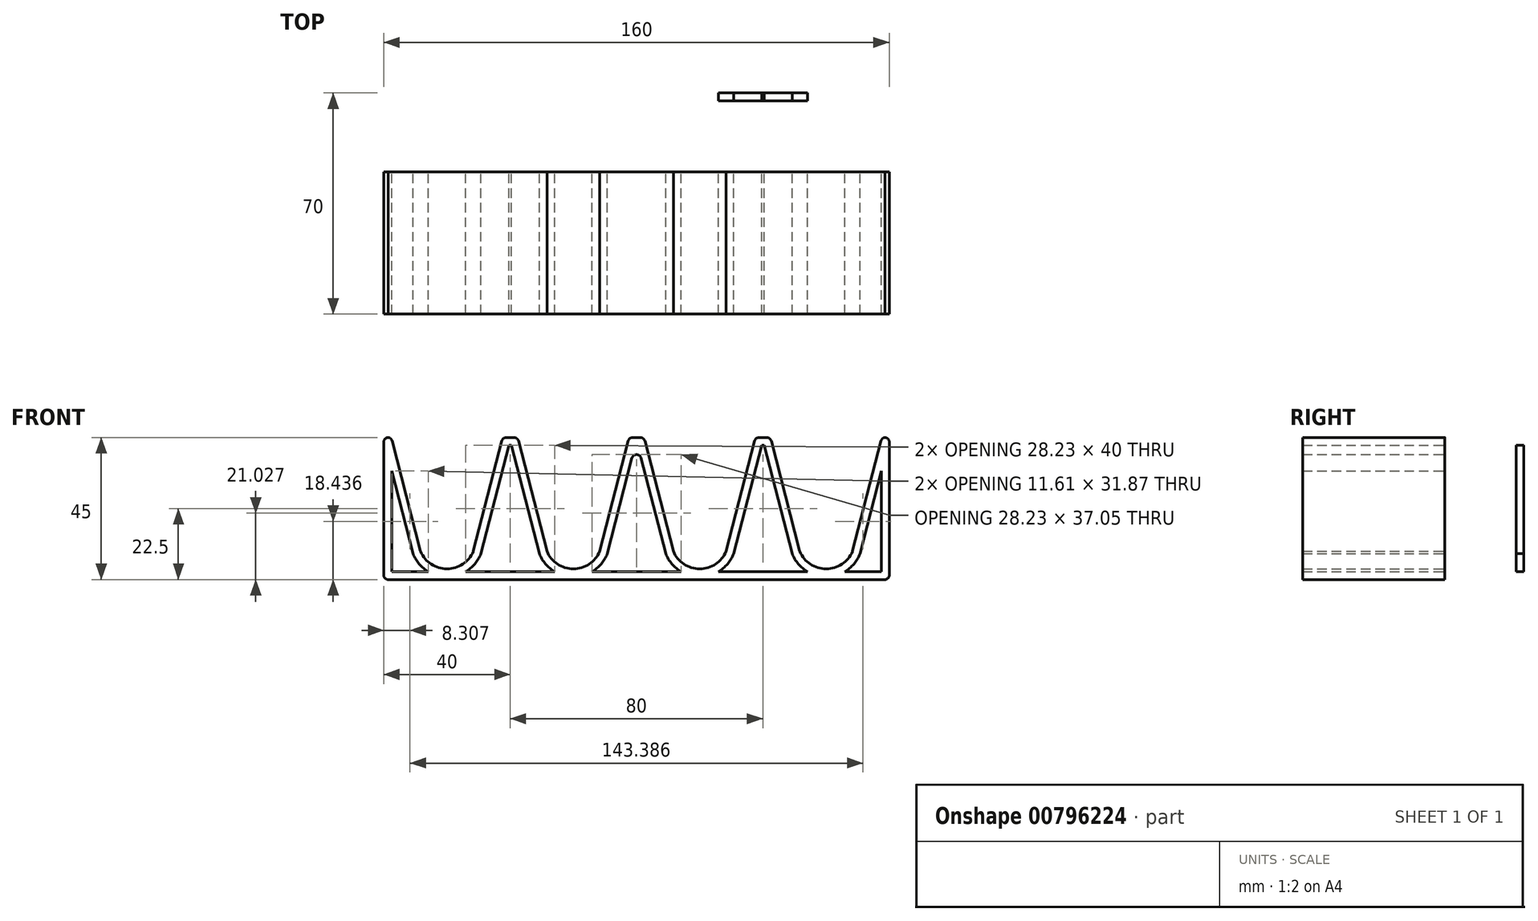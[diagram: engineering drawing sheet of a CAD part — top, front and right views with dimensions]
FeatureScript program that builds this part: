
annotation { "Feature Type Name" : "Feature", "Feature Type Description" : "" }
export const myFeature = defineFeature(function(context is Context, id is Id, definition is map)
    precondition{}
    {
        {
            var Q0;
            Q0=qCreatedBy(makeId("Front.planeOp"),FACE);
            var sketch = newSketch(context, id + "F0", { "sketchPlane" : qUnion([Q0])});
            skLineSegment(sketch, "E0.bottom", {"start": v(0, 0) * mm, "end": v(-80, 0) * mm});
            skLineSegment(sketch, "E0.top", {"start": v(0, 45) * mm, "end": v(-80, 45) * mm});
            skLineSegment(sketch, "E0.left", {"start": v(0, 0) * mm, "end": v(0, 45) * mm});
            skLineSegment(sketch, "E0.right", {"start": v(-80, 0) * mm, "end": v(-80, 45) * mm});
            skLineSegment(sketch, "E1", {"start": v(-40, 45) * mm, "end": v(-40, 0) * mm});
            skLineSegment(sketch, "E2", {"start": v(-80, 45) * mm, "end": v(-40, 45) * mm});
            skLineSegment(sketch, "E3", {"start": v(-60, 45) * mm, "end": v(-60, 0) * mm});
            skLineSegment(sketch, "E4", {"start": v(-77.66, 45) * mm, "end": v(-68.36, 8.98) * mm});
            skLineSegment(sketch, "E5.MirrorCS", {"start": v(-42.34, 45) * mm, "end": v(-51.64, 8.98) * mm});
            skArc(sketch, "E6", {"start": v(-68.36, 8.98) * mm, "mid": v(-60, 3.39) * mm, "end": v(-51.64, 8.98) * mm});
            skLineSegment(sketch, "E7.MirrorCS", {"start": v(-37.66, 45) * mm, "end": v(-28.36, 8.98) * mm});
            skLineSegment(sketch, "E8.MirrorCS", {"start": v(-2.34, 45) * mm, "end": v(-11.64, 8.98) * mm});
            skLineSegment(sketch, "E9.MirrorCS", {"start": v(-20, 45) * mm, "end": v(-20, 0) * mm});
            skArc(sketch, "E10.MirrorCS", {"start": v(-11.64, 8.98) * mm, "mid": v(-20, 3.39) * mm, "end": v(-28.36, 8.98) * mm});
            skSolve(sketch);
        }
        {
            var Q0;
            {var subQ6=sQuery(id+"F0.wireOp",EDGE,"E0.right");Q0=makeQuery(id+"F0.imprint","IMPRINT",FACE,{"disambiguationData":[TD([[makeQuery(id+"F0.imprint","IMPRINT",EDGE,{"derivedFrom":subQ6}),-1.0]])]});}
            var Q1;
            {var subQ6=sQuery(id+"F0.wireOp",EDGE,"E1");Q1=makeQuery(id+"F0.imprint","IMPRINT",FACE,{"disambiguationData":[TD([[makeQuery(id+"F0.imprint","IMPRINT",EDGE,{"derivedFrom":subQ6}),-1.0]])]});}
            var Q2;
            {var subQ0=sQuery(id+"F0.wireOp",EDGE,"E1");Q2=makeQuery(id+"F0.imprint","IMPRINT",FACE,{"disambiguationData":[TD([[makeQuery(id+"F0.imprint","IMPRINT",EDGE,{"derivedFrom":subQ0}),1.0]])]});}
            var Q3;
            {var subQ1=sQuery(id+"F0.wireOp",EDGE,"E0.left");Q3=makeQuery(id+"F0.imprint","IMPRINT",FACE,{"disambiguationData":[TD([[makeQuery(id+"F0.imprint","IMPRINT",EDGE,{"derivedFrom":subQ1}),1.0]])]});}
            extrude(context, id + "F1", {"entities" : qUnion([Q0, Q1, Q2, Q3]), "depth" : 70 * mm, "offsetDistance" : 25 * mm});
        }
        {
            var Q0;
            Q0=makeQuery(id+"F1.opExtrude","CAP_FACE",FACE,{"disambiguationData":[OSD([sQuery(id+"F0.wireOp",EDGE,"E0.bottom"),sQuery(id+"F0.wireOp",EDGE,"E0.top"),sQuery(id+"F0.wireOp",EDGE,"E0.left"),sQuery(id+"F0.wireOp",EDGE,"E0.right"),sQuery(id+"F0.wireOp",EDGE,"E2"),sQuery(id+"F0.wireOp",EDGE,"E4"),sQuery(id+"F0.wireOp",EDGE,"E5.MirrorCS"),sQuery(id+"F0.wireOp",EDGE,"E6"),sQuery(id+"F0.wireOp",EDGE,"E7.MirrorCS"),sQuery(id+"F0.wireOp",EDGE,"E8.MirrorCS"),sQuery(id+"F0.wireOp",EDGE,"E10.MirrorCS")])],"isStart":false});
            shell(context, id + "F2", {"entities" : qUnion([Q0]), "thickness" : 2.5 * mm});
        }
        {
            var Q0;
            Q0=makeQuery(id+"F1.opExtrude","SWEPT_BODY",BODY,{"disambiguationData":[OSD([sQuery(id+"F0.wireOp",EDGE,"E0.bottom"),sQuery(id+"F0.wireOp",EDGE,"E0.top"),sQuery(id+"F0.wireOp",EDGE,"E0.left"),sQuery(id+"F0.wireOp",EDGE,"E0.right"),sQuery(id+"F0.wireOp",EDGE,"E2"),sQuery(id+"F0.wireOp",EDGE,"E4"),sQuery(id+"F0.wireOp",EDGE,"E5.MirrorCS"),sQuery(id+"F0.wireOp",EDGE,"E6"),sQuery(id+"F0.wireOp",EDGE,"E7.MirrorCS"),sQuery(id+"F0.wireOp",EDGE,"E8.MirrorCS"),sQuery(id+"F0.wireOp",EDGE,"E10.MirrorCS")])]});
            var Q1;
            Q1=makeQuery(id+"F1.opExtrude","SWEPT_FACE",FACE,{"disambiguationData":[OSD([sQuery(id+"F0.wireOp",EDGE,"E0.left")])]});
            mirror(context, id + "F3", {"operationType" : NewBodyOperationType.ADD, "entities" : qUnion([Q0]), "mirrorPlane" : qUnion([Q1])});
        }
        {
            var Q0;
            {var subQ0=makeQuery(id+"F1.opExtrude","CAP_FACE",FACE,{"disambiguationData":[OSD([sQuery(id+"F0.wireOp",EDGE,"E0.bottom"),sQuery(id+"F0.wireOp",EDGE,"E0.top"),sQuery(id+"F0.wireOp",EDGE,"E0.left"),sQuery(id+"F0.wireOp",EDGE,"E0.right"),sQuery(id+"F0.wireOp",EDGE,"E2"),sQuery(id+"F0.wireOp",EDGE,"E4"),sQuery(id+"F0.wireOp",EDGE,"E5.MirrorCS"),sQuery(id+"F0.wireOp",EDGE,"E6"),sQuery(id+"F0.wireOp",EDGE,"E7.MirrorCS"),sQuery(id+"F0.wireOp",EDGE,"E8.MirrorCS"),sQuery(id+"F0.wireOp",EDGE,"E10.MirrorCS")])],"isStart":false});Q0=makeQuery(id+"F3.boolean.opBoolean","MERGE",FACE,{"derivedFrom":[subQ0,makeQuery(id+"F3.opPattern","COPY",FACE,{"derivedFrom":subQ0,"instanceName":"1"})]});}
            var sketch = newSketch(context, id + "F4", { "sketchPlane" : qUnion([Q0])});
            skLineSegment(sketch, "E11.0.0", {"start": v(2.5, 2.5) * mm, "end": v(14.11, 2.5) * mm});
            skArc(sketch, "E11.0.1", {"start": v(9.26, 8.2) * mm, "mid": v(11.21, 4.94) * mm, "end": v(14.11, 2.5) * mm});
            skLineSegment(sketch, "E11.0.2", {"start": v(9.26, 8.2) * mm, "end": v(2.5, 34.37) * mm});
            skLineSegment(sketch, "E11.0.3", {"start": v(2.5, 34.37) * mm, "end": v(2.5, 2.5) * mm});
            skArc(sketch, "E12.0.0", {"start": v(-11.64, 8.98) * mm, "mid": v(-20, 3.39) * mm, "end": v(-28.36, 8.98) * mm});
            skLineSegment(sketch, "E12.0.1", {"start": v(-28.36, 8.98) * mm, "end": v(-28.36, 0) * mm});
            skLineSegment(sketch, "E12.0.2", {"start": v(-28.36, 0) * mm, "end": v(0, 0) * mm});
            skLineSegment(sketch, "E12.0.3", {"start": v(0, 0) * mm, "end": v(0, 45) * mm});
            skLineSegment(sketch, "E12.0.4", {"start": v(0, 45) * mm, "end": v(-2.34, 45) * mm});
            skLineSegment(sketch, "E12.0.5", {"start": v(-2.34, 45) * mm, "end": v(-11.64, 8.98) * mm});
            skLineSegment(sketch, "E13.0", {"start": v(-2.5, 2.5) * mm, "end": v(-2.5, 34.37) * mm});
            skLineSegment(sketch, "E14.0.0", {"start": v(-80, 0) * mm, "end": v(80, 0) * mm});
            skLineSegment(sketch, "E14.0.1", {"start": v(80, 0) * mm, "end": v(80, 45) * mm});
            skLineSegment(sketch, "E14.0.2", {"start": v(80, 45) * mm, "end": v(77.66, 45) * mm});
            skLineSegment(sketch, "E14.0.3", {"start": v(77.66, 45) * mm, "end": v(68.36, 8.98) * mm});
            skArc(sketch, "E14.0.4", {"start": v(68.36, 8.98) * mm, "mid": v(60, 3.39) * mm, "end": v(51.64, 8.98) * mm});
            skLineSegment(sketch, "E14.0.5", {"start": v(51.64, 8.98) * mm, "end": v(42.34, 45) * mm});
            skLineSegment(sketch, "E14.0.6", {"start": v(42.34, 45) * mm, "end": v(37.66, 45) * mm});
            skLineSegment(sketch, "E14.0.7", {"start": v(37.66, 45) * mm, "end": v(28.36, 8.98) * mm});
            skArc(sketch, "E14.0.8", {"start": v(28.36, 8.98) * mm, "mid": v(20, 3.39) * mm, "end": v(11.64, 8.98) * mm});
            skLineSegment(sketch, "E14.0.9", {"start": v(11.64, 8.98) * mm, "end": v(2.34, 45) * mm});
            skLineSegment(sketch, "E14.0.10", {"start": v(2.34, 45) * mm, "end": v(-2.34, 45) * mm});
            skLineSegment(sketch, "E14.0.13", {"start": v(-28.36, 8.98) * mm, "end": v(-37.66, 45) * mm});
            skLineSegment(sketch, "E14.0.14", {"start": v(-37.66, 45) * mm, "end": v(-42.34, 45) * mm});
            skLineSegment(sketch, "E14.0.15", {"start": v(-42.34, 45) * mm, "end": v(-51.64, 8.98) * mm});
            skArc(sketch, "E14.0.16", {"start": v(-51.64, 8.98) * mm, "mid": v(-60, 3.39) * mm, "end": v(-68.36, 8.98) * mm});
            skLineSegment(sketch, "E14.0.17", {"start": v(-68.36, 8.98) * mm, "end": v(-77.66, 45) * mm});
            skLineSegment(sketch, "E14.0.18", {"start": v(-77.66, 45) * mm, "end": v(-80, 45) * mm});
            skLineSegment(sketch, "E14.0.19", {"start": v(-80, 45) * mm, "end": v(-80, 0) * mm});
            skLineSegment(sketch, "E15", {"start": v(-2.5, 34.37) * mm, "end": v(0, 44.06) * mm});
            skLineSegment(sketch, "E16", {"start": v(0, 44.06) * mm, "end": v(2.5, 34.37) * mm});
            skLineSegment(sketch, "E17", {"start": v(-2.5, 2.5) * mm, "end": v(2.5, 2.5) * mm});
            skSolve(sketch);
        }
        {
            var Q0;
            {var subQ4=sQuery(id+"F4.wireOp",EDGE,"E13.0");Q0=makeQuery(id+"F4.imprint","IMPRINT",FACE,{"disambiguationData":[TD([[makeQuery(id+"F4.imprint","IMPRINT",EDGE,{"derivedFrom":subQ4}),-1.0]])]});}
            var Q1;
            {var subQ0=sQuery(id+"F4.wireOp",EDGE,"E11.0.3");Q1=makeQuery(id+"F4.imprint","IMPRINT",FACE,{"disambiguationData":[TD([[makeQuery(id+"F4.imprint","IMPRINT",EDGE,{"derivedFrom":subQ0}),1.0]])]});}
            extrude(context, id + "F5", {"entities" : qUnion([Q0, Q1]), "operationType" : NewBodyOperationType.REMOVE, "oppositeDirection" : true, "depth" : 97.5 * mm, "offsetDistance" : 25 * mm});
        }
        {
            var Q0;
            {var subQ0=makeQuery(id+"F1.opExtrude","CAP_FACE",FACE,{"disambiguationData":[OSD([sQuery(id+"F0.wireOp",EDGE,"E0.bottom"),sQuery(id+"F0.wireOp",EDGE,"E0.top"),sQuery(id+"F0.wireOp",EDGE,"E0.left"),sQuery(id+"F0.wireOp",EDGE,"E0.right"),sQuery(id+"F0.wireOp",EDGE,"E2"),sQuery(id+"F0.wireOp",EDGE,"E4"),sQuery(id+"F0.wireOp",EDGE,"E5.MirrorCS"),sQuery(id+"F0.wireOp",EDGE,"E6"),sQuery(id+"F0.wireOp",EDGE,"E7.MirrorCS"),sQuery(id+"F0.wireOp",EDGE,"E8.MirrorCS"),sQuery(id+"F0.wireOp",EDGE,"E10.MirrorCS")])],"isStart":true});Q0=makeQuery(id+"F3.boolean.opBoolean","MERGE",FACE,{"derivedFrom":[subQ0,makeQuery(id+"F3.opPattern","COPY",FACE,{"derivedFrom":subQ0,"instanceName":"1"})]});}
            var sketch = newSketch(context, id + "F6", { "sketchPlane" : qUnion([Q0])});
            skArc(sketch, "E18.0.0", {"start": v(25.89, 2.5) * mm, "mid": v(28.79, 4.94) * mm, "end": v(30.74, 8.2) * mm});
            skLineSegment(sketch, "E18.0.1", {"start": v(30.74, 8.2) * mm, "end": v(39.6, 42.5) * mm});
            skLineSegment(sketch, "E18.0.2", {"start": v(39.6, 42.5) * mm, "end": v(40.4, 42.5) * mm});
            skLineSegment(sketch, "E18.0.3", {"start": v(40.4, 42.5) * mm, "end": v(49.26, 8.2) * mm});
            skArc(sketch, "E18.0.4", {"start": v(49.26, 8.2) * mm, "mid": v(51.21, 4.94) * mm, "end": v(54.11, 2.5) * mm});
            skLineSegment(sketch, "E18.0.5", {"start": v(54.11, 2.5) * mm, "end": v(25.89, 2.5) * mm});
            skArc(sketch, "E19.0.0", {"start": v(65.89, 2.5) * mm, "mid": v(68.79, 4.94) * mm, "end": v(70.74, 8.2) * mm});
            skLineSegment(sketch, "E19.0.1", {"start": v(70.74, 8.2) * mm, "end": v(77.5, 34.37) * mm});
            skLineSegment(sketch, "E19.0.2", {"start": v(77.5, 34.37) * mm, "end": v(77.5, 2.5) * mm});
            skLineSegment(sketch, "E19.0.3", {"start": v(77.5, 2.5) * mm, "end": v(65.89, 2.5) * mm});
            skLineSegment(sketch, "E20.0.0", {"start": v(14.11, 2.5) * mm, "end": v(-14.11, 2.5) * mm});
            skArc(sketch, "E20.0.1", {"start": v(-9.26, 8.2) * mm, "mid": v(-11.21, 4.94) * mm, "end": v(-14.11, 2.5) * mm});
            skLineSegment(sketch, "E20.0.2", {"start": v(-9.26, 8.2) * mm, "end": v(0, 44.06) * mm});
            skLineSegment(sketch, "E20.0.3", {"start": v(0, 44.06) * mm, "end": v(9.26, 8.2) * mm});
            skArc(sketch, "E20.0.4", {"start": v(9.26, 8.2) * mm, "mid": v(11.21, 4.94) * mm, "end": v(14.11, 2.5) * mm});
            skArc(sketch, "E21.0.0", {"start": v(-25.89, 2.5) * mm, "mid": v(-28.79, 4.94) * mm, "end": v(-30.74, 8.2) * mm});
            skLineSegment(sketch, "E21.0.1", {"start": v(-25.89, 2.5) * mm, "end": v(-54.11, 2.5) * mm});
            skArc(sketch, "E21.0.2", {"start": v(-54.11, 2.5) * mm, "mid": v(-51.21, 4.94) * mm, "end": v(-49.26, 8.2) * mm});
            skLineSegment(sketch, "E21.0.3", {"start": v(-49.26, 8.2) * mm, "end": v(-40.4, 42.5) * mm});
            skLineSegment(sketch, "E21.0.4", {"start": v(-40.4, 42.5) * mm, "end": v(-39.6, 42.5) * mm});
            skLineSegment(sketch, "E21.0.5", {"start": v(-39.6, 42.5) * mm, "end": v(-30.74, 8.2) * mm});
            skArc(sketch, "E22.0.0", {"start": v(-70.74, 8.2) * mm, "mid": v(-68.79, 4.94) * mm, "end": v(-65.89, 2.5) * mm});
            skLineSegment(sketch, "E22.0.1", {"start": v(-65.89, 2.5) * mm, "end": v(-77.5, 2.5) * mm});
            skLineSegment(sketch, "E22.0.2", {"start": v(-77.5, 2.5) * mm, "end": v(-77.5, 34.37) * mm});
            skLineSegment(sketch, "E22.0.3", {"start": v(-77.5, 34.37) * mm, "end": v(-70.74, 8.2) * mm});
            skSolve(sketch);
        }
        {
            var Q0;
            Q0=makeQuery(id+"F6.imprint","IMPRINT",FACE,{"disambiguationData":[TD([[makeQuery(id+"F6.imprint","IMPRINT",EDGE,{"derivedFrom":sQuery(id+"F6.wireOp",EDGE,"E22.0.0")}),-1.0]])]});
            var Q1;
            Q1=makeQuery(id+"F6.imprint","IMPRINT",FACE,{"disambiguationData":[TD([[makeQuery(id+"F6.imprint","IMPRINT",EDGE,{"derivedFrom":sQuery(id+"F6.wireOp",EDGE,"E21.0.0")}),1.0]])]});
            var Q2;
            Q2=makeQuery(id+"F6.imprint","IMPRINT",FACE,{"disambiguationData":[TD([[makeQuery(id+"F6.imprint","IMPRINT",EDGE,{"derivedFrom":sQuery(id+"F6.wireOp",EDGE,"E20.0.0")}),-1.0]])]});
            var Q3;
            Q3=makeQuery(id+"F6.imprint","IMPRINT",FACE,{"disambiguationData":[TD([[makeQuery(id+"F6.imprint","IMPRINT",EDGE,{"derivedFrom":sQuery(id+"F6.wireOp",EDGE,"E18.0.0")}),-1.0]])]});
            var Q4;
            Q4=makeQuery(id+"F6.imprint","IMPRINT",FACE,{"disambiguationData":[TD([[makeQuery(id+"F6.imprint","IMPRINT",EDGE,{"derivedFrom":sQuery(id+"F6.wireOp",EDGE,"E19.0.0")}),-1.0]])]});
            extrude(context, id + "F7", {"entities" : qUnion([Q0, Q1, Q2, Q3, Q4]), "operationType" : NewBodyOperationType.REMOVE, "oppositeDirection" : true, "depth" : 25 * mm, "offsetDistance" : 25 * mm});
        }
        {
            var Q0;
            Q0=makeQuery(id+"F1.opExtrude","SWEPT_EDGE",EDGE,{"disambiguationData":[OSD([sQuery(id+"F0.wireOp",EDGE,"E0.right"),sQuery(id+"F0.wireOp",EDGE,"E2")])]});
            var Q1;
            Q1=makeQuery(id+"F1.opExtrude","SWEPT_EDGE",EDGE,{"disambiguationData":[OSD([sQuery(id+"F0.wireOp",EDGE,"E2"),sQuery(id+"F0.wireOp",EDGE,"E4")])]});
            var Q2;
            Q2=makeQuery(id+"F1.opExtrude","SWEPT_EDGE",EDGE,{"disambiguationData":[OSD([sQuery(id+"F0.wireOp",EDGE,"E2"),sQuery(id+"F0.wireOp",EDGE,"E5.MirrorCS")])]});
            var Q3;
            Q3=makeQuery(id+"F1.opExtrude","SWEPT_EDGE",EDGE,{"disambiguationData":[OSD([sQuery(id+"F0.wireOp",EDGE,"E0.top"),sQuery(id+"F0.wireOp",EDGE,"E7.MirrorCS")])]});
            var Q4;
            Q4=makeQuery(id+"F3.opPattern","COPY",EDGE,{"derivedFrom":makeQuery(id+"F1.opExtrude","SWEPT_EDGE",EDGE,{"disambiguationData":[OSD([sQuery(id+"F0.wireOp",EDGE,"E0.top"),sQuery(id+"F0.wireOp",EDGE,"E8.MirrorCS")])]}),"instanceName":"1"});
            var Q5;
            Q5=makeQuery(id+"F1.opExtrude","SWEPT_EDGE",EDGE,{"disambiguationData":[OSD([sQuery(id+"F0.wireOp",EDGE,"E0.top"),sQuery(id+"F0.wireOp",EDGE,"E8.MirrorCS")])]});
            var Q6;
            Q6=makeQuery(id+"F3.opPattern","COPY",EDGE,{"derivedFrom":makeQuery(id+"F1.opExtrude","SWEPT_EDGE",EDGE,{"disambiguationData":[OSD([sQuery(id+"F0.wireOp",EDGE,"E0.top"),sQuery(id+"F0.wireOp",EDGE,"E7.MirrorCS")])]}),"instanceName":"1"});
            var Q7;
            Q7=makeQuery(id+"F3.opPattern","COPY",EDGE,{"derivedFrom":makeQuery(id+"F1.opExtrude","SWEPT_EDGE",EDGE,{"disambiguationData":[OSD([sQuery(id+"F0.wireOp",EDGE,"E2"),sQuery(id+"F0.wireOp",EDGE,"E5.MirrorCS")])]}),"instanceName":"1"});
            var Q8;
            Q8=makeQuery(id+"F3.opPattern","COPY",EDGE,{"derivedFrom":makeQuery(id+"F1.opExtrude","SWEPT_EDGE",EDGE,{"disambiguationData":[OSD([sQuery(id+"F0.wireOp",EDGE,"E2"),sQuery(id+"F0.wireOp",EDGE,"E4")])]}),"instanceName":"1"});
            var Q9;
            Q9=makeQuery(id+"F3.opPattern","COPY",EDGE,{"derivedFrom":makeQuery(id+"F1.opExtrude","SWEPT_EDGE",EDGE,{"disambiguationData":[OSD([sQuery(id+"F0.wireOp",EDGE,"E0.right"),sQuery(id+"F0.wireOp",EDGE,"E2")])]}),"instanceName":"1"});
            var Q10;
            Q10=makeQuery(id+"F7.boolean.opBoolean","MERGE",EDGE,{"derivedFrom":[makeQuery(id+"F5.boolean.opBoolean","COPY",EDGE,{"derivedFrom":makeQuery(id+"F5.opExtrude","SWEPT_EDGE",EDGE,{"disambiguationData":[OSD([sQuery(id+"F4.wireOp",EDGE,"E12.0.3"),sQuery(id+"F4.wireOp",EDGE,"E15"),sQuery(id+"F4.wireOp",EDGE,"E16")])]})}),makeQuery(id+"F7.opExtrude","SWEPT_EDGE",EDGE,{"disambiguationData":[OSD([sQuery(id+"F6.wireOp",EDGE,"E20.0.2"),sQuery(id+"F6.wireOp",EDGE,"E20.0.3")])]})]});
            fillet(context, id + "F8", {"entities" : qUnion([Q0, Q1, Q2, Q3, Q4, Q5, Q6, Q7, Q8, Q9, Q10]), "radius" : 1.5 * mm, "tangentPropagation" : true, "allowEdgeOverflow" : false});
        }
    });
